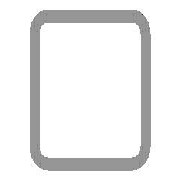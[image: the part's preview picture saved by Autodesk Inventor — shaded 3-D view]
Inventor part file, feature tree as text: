
AUTODESK INVENTOR PART (.ipt)
format: ipt  version: 2022 (Build 260153000, 153)  size: 287,744 bytes
history: native  units: mm (DEFAULTED — no unit token found)
features: plane x7, other x5, sketch x4, extrude x2, boolean_combine x2, sweep x1
ambient origin geometry x8: Origin, YZ Plane, XZ Plane, XY Plane, X Axis, Y Axis, Z Axis, Center Point
bodies: Solid1 (feature_tree), Body (feature_tree), Solid2 (feature_tree), Solid3 (feature_tree)
feature tree (21):
  parser-record x1  (decoder bookkeeping rows leaked as tree rows — omitted from the tree; the rows remain in map.json)
  other  "Driven Length"
  other  "Start Plane"
  other  "End Plane"
  sweep  "Sweep Path"
  other  "Orientation Work Plane"
  plane  "Work Plane5"
  plane  "Work Plane6"
  plane  "Work Plane7"
  extrude  "Extrusion2"  Depth=2.0mm
  boolean_combine  "Combine1"
  plane  "Work Plane8"
  plane  "Work Plane9"
  plane  "Work Plane10"
  extrude  "Extrusion3"  Depth=2899.411255mm
  boolean_combine  "Combine2"
  sketch  "Sketch3"  dims[d7=4.0mm d9=40.0mm]
  plane  "Work Plane3"
  sketch  "Sketch4"  dims[d11=40.0mm d12=2.0mm]
  sketch  "Sketch5"  dims[d13=-0.0mm d14=2899.411255mm]
  sketch  "Sketch6"  dims[d15=20.0mm d16=20.0mm d17=90.0deg d18=2899.411255mm d19=0.0mm d20=0.0mm d21=0.12mm d22=0.0mm d23=0.12mm d24=0.0mm]
